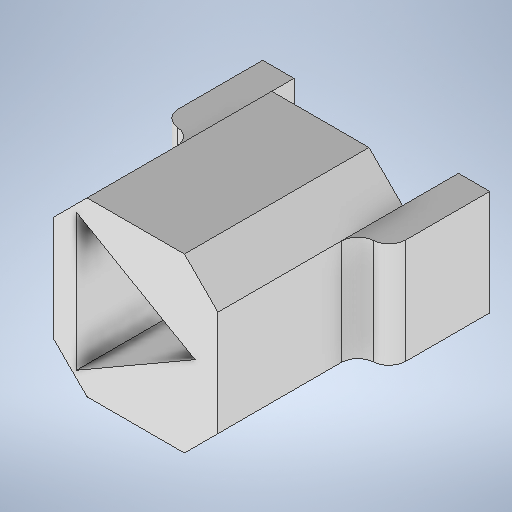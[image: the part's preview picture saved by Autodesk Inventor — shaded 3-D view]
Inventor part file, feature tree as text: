
AUTODESK INVENTOR PART (.ipt)
format: ipt  version: 2025.1 (Build 291241000, 241)  size: 308,224 bytes
history: native  units: mm
features: extrude x5, sketch x3, chamfer x1, fillet x1, projected_geometry x1
ambient origin geometry x8: Origin, YZ Plane, XZ Plane, XY Plane, X Axis, Y Axis, Z Axis, Center Point
bodies: Solid1 (feature_tree)
feature tree (11):
  sketch  "Sketch1"  dims[d0=29.4mm d1=18.8mm]
  extrude  "Extrusion1"  Depth=18.8mm
  extrude  "Extrusion2"  Depth=14.7mm
  sketch  "Sketch2"  dims[d2=9.4mm d3=14.7mm]
  extrude  "Extrusion3"  Depth=5.6mm
  extrude  "Extrusion4"  Depth=18.0mm TaperAngle=0.0deg
  chamfer  "Chamfer1"  Distance=10.0mm
  fillet  "Fillet1"  Radius=21.2mm
  extrude  "Extrusion5"  TaperAngle=0.0deg  [1 undecoded]
  sketch  "Sketch4"  dims[d4=5.6mm d5=5.6mm d6=18.0mm d7=0.0mm d8=10.0mm d9=0.0mm d17=21.2mm d18=0.0mm d19=21.2mm d20=21.2mm d21=10.6mm d25=6.0mm d26=6.0mm d27=0.0mm d28=0.0mm d29=10.0mm d30=8.0mm d31=0.0mm d32=0.0mm d33=8.0mm d34=0.0mm d35=6.0mm d36=2.0mm d37=45.0deg d38=3.0mm d39=15.0mm d40=0.0mm]
  projected_geometry  "Projected Loop1"
note: 1 required parameter value undecoded (feature->parameter linkage not recoverable at this tier; creation-order binding heuristic only, values carry confidence <= 0.55)
